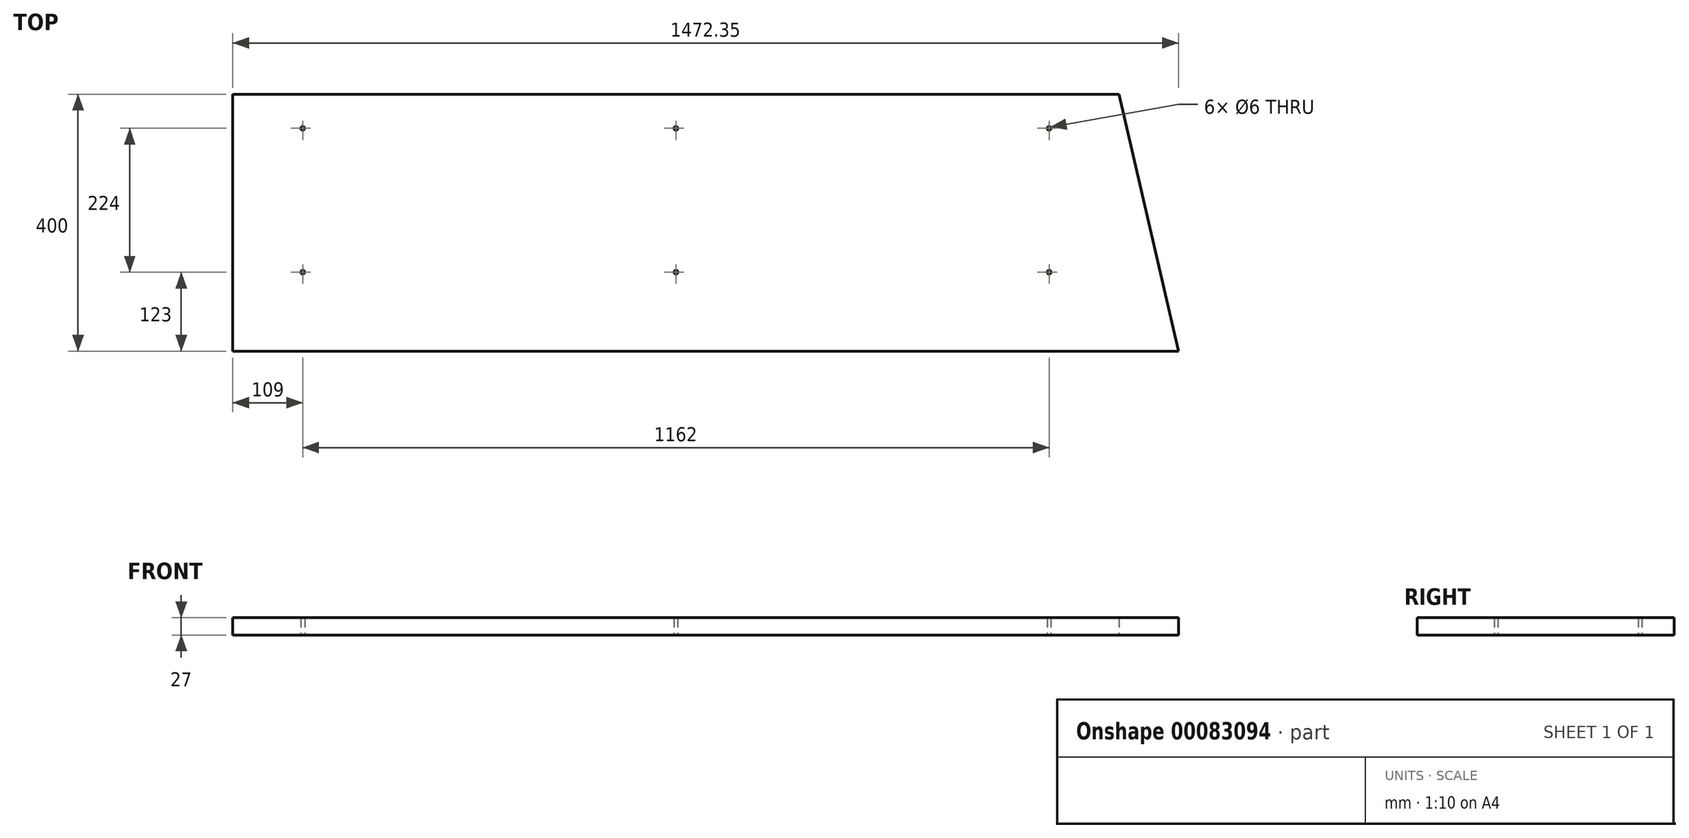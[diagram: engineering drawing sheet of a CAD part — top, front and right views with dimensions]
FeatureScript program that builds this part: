
annotation { "Feature Type Name" : "Feature", "Feature Type Description" : "" }
export const myFeature = defineFeature(function(context is Context, id is Id, definition is map)
    precondition{}
    {
        {
            var Q0;
            Q0=qCreatedBy(makeId("Top.planeOp"),FACE);
            var sketch = newSketch(context, id + "F0", { "sketchPlane" : qUnion([Q0])});
            skLineSegment(sketch, "E0.bottom", {"start": v(0, 0) * mm, "end": v(1380, 0) * mm});
            skLineSegment(sketch, "E0.top", {"start": v(0, 400) * mm, "end": v(1380, 400) * mm});
            skLineSegment(sketch, "E0.left", {"start": v(0, 0) * mm, "end": v(0, 400) * mm});
            skLineSegment(sketch, "E0.right", {"start": v(1380, 0) * mm, "end": v(1380, 400) * mm});
            skLineSegment(sketch, "E1", {"start": v(1472.35, 0) * mm, "end": v(1380, 400) * mm});
            skLineSegment(sketch, "E2", {"start": v(1472.35, 0) * mm, "end": v(1380, 0) * mm});
            skSolve(sketch);
        }
        {
            var Q0;
            Q0 = qSketchRegion(id + "F0", true);
            extrude(context, id + "F1", {"entities" : qUnion([Q0]), "depth" : 27 * mm});
        }
        {
            var Q0;
            Q0=makeQuery(id+"F1.opExtrude","CAP_FACE",FACE,{"disambiguationData":[OSD([sQuery(id+"F0.wireOp",EDGE,"E0.bottom"),sQuery(id+"F0.wireOp",EDGE,"E0.top"),sQuery(id+"F0.wireOp",EDGE,"E0.left"),sQuery(id+"F0.wireOp",EDGE,"E0.right")])],"isStart":true});
            var sketch = newSketch(context, id + "F2", { "sketchPlane" : qUnion([Q0])});
            skCircle(sketch, "E3", {"center": v(690, -123) * mm, "radius": 3 * mm});
            skCircle(sketch, "E4", {"center": v(690, -347) * mm, "radius": 3 * mm});
            skCircle(sketch, "E5", {"center": v(109, -123) * mm, "radius": 3 * mm});
            skCircle(sketch, "E6", {"center": v(109, -347) * mm, "radius": 3 * mm});
            skCircle(sketch, "E7", {"center": v(1271, -123) * mm, "radius": 3 * mm});
            skCircle(sketch, "E8", {"center": v(1271, -347) * mm, "radius": 3 * mm});
            skSolve(sketch);
        }
        {
            var Q0;
            Q0=makeQuery(id+"F2.imprint","IMPRINT",FACE,{"disambiguationData":[TD([[makeQuery(id+"F2.imprint","IMPRINT",EDGE,{"derivedFrom":sQuery(id+"F2.wireOp",EDGE,"E7")}),1.0]])]});
            var Q1;
            Q1=makeQuery(id+"F2.imprint","IMPRINT",FACE,{"disambiguationData":[TD([[makeQuery(id+"F2.imprint","IMPRINT",EDGE,{"derivedFrom":sQuery(id+"F2.wireOp",EDGE,"E8")}),1.0]])]});
            var Q2;
            Q2=makeQuery(id+"F2.imprint","IMPRINT",FACE,{"disambiguationData":[TD([[makeQuery(id+"F2.imprint","IMPRINT",EDGE,{"derivedFrom":sQuery(id+"F2.wireOp",EDGE,"E5")}),1.0]])]});
            var Q3;
            Q3=makeQuery(id+"F2.imprint","IMPRINT",FACE,{"disambiguationData":[TD([[makeQuery(id+"F2.imprint","IMPRINT",EDGE,{"derivedFrom":sQuery(id+"F2.wireOp",EDGE,"E6")}),1.0]])]});
            var Q4;
            Q4=makeQuery(id+"F2.imprint","IMPRINT",FACE,{"disambiguationData":[TD([[makeQuery(id+"F2.imprint","IMPRINT",EDGE,{"derivedFrom":sQuery(id+"F2.wireOp",EDGE,"E4")}),1.0]])]});
            var Q5;
            Q5=makeQuery(id+"F2.imprint","IMPRINT",FACE,{"disambiguationData":[TD([[makeQuery(id+"F2.imprint","IMPRINT",EDGE,{"derivedFrom":sQuery(id+"F2.wireOp",EDGE,"E3")}),1.0]])]});
            extrude(context, id + "F3", {"entities" : qUnion([Q0, Q1, Q2, Q3, Q4, Q5]), "operationType" : NewBodyOperationType.REMOVE, "endBound" : BoundingType.THROUGH_ALL, "oppositeDirection" : true, "depth" : 10 * mm});
        }
    });
